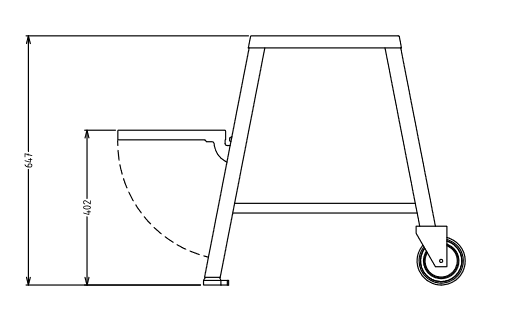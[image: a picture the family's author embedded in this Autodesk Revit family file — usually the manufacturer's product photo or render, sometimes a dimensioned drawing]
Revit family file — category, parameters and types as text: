
# Revit family: QF_ELECTROLUXPROFESSIONAL_653180_TT11
name_source: partatom
category: Attrezzature speciali
units: mm (PartAtom-declared; Revit-internal decimal feet)

## family parameters
Basato su piano di lavoro = No
Condiviso = No
Punto di calcolo locali = No
Quota connettore circolare = Usa diametro
Sempre verticale = Sì
Taglio con vuoti quando caricato = No
Tipo di parte = Normale

## types (1)
- Standard
    Accessory = Sì
    Cold Water Size = 0 mm
    Compressed Air Pressure = 0.0 Pa
    Compressed Air Size = 0 mm
    Compressed Air Volume = 0.0 L/s
    Condensate Return Size = 0 mm
    Cycle = 0 Hz
    Depth Actual = 690 mm  [stored 2.26378 ft]
    Descrizione = TABLE+SHELF+GN 1/1 POLYCARBONATE TRAY
    Direct Waste Size = 0 mm
    Gas Input Pressure = 0
    Gas KW = 0
    Gas Size = 0 mm
    HP = 0 HP
    Height Actual = 576 mm  [stored 1.88976 ft]
    Hot Water Size = 0 mm
    Item Number = 653180
    Length Actual = 445 mm  [stored 1.45997 ft]
    Modello = TT11
    Phase = 0
    Produttore = Electrolux Professional
    Prospetto di default = 0 mm  [stored 0 ft]
    Refrigerant Compressor Remote = Sì
    Refrigeration Liquid Line Size = 0 mm  [stored 0 ft]
    Refrigeration Suction Line Size = 0 mm  [stored 0 ft]
    Steam Consumption per Hour = 0
    Steam Supply Maximum Pressure = 0.0 Pa
    Steam Supply Minimum Pressure = 0.0 Pa
    Steam Supply Size = 0 mm
    URL = https://www.electroluxprofessional.com
    URL Manufacturer = https://www.electroluxprofessional.com
    Volts = 0 V
    Watts = 0 W
    Weight = 14.00 kg

note: source unit labels omitted for Gas Input Pressure — the stored unit's dimension contradicts the parameter name (converter mislabeling)

note: [stored X ft] marks values corroborated as IEEE doubles in the binary element streams (Revit-internal decimal feet)

## geometry (parser evidence)
native form markers: Sweep x2
no freeform markers — native parametric forms only
